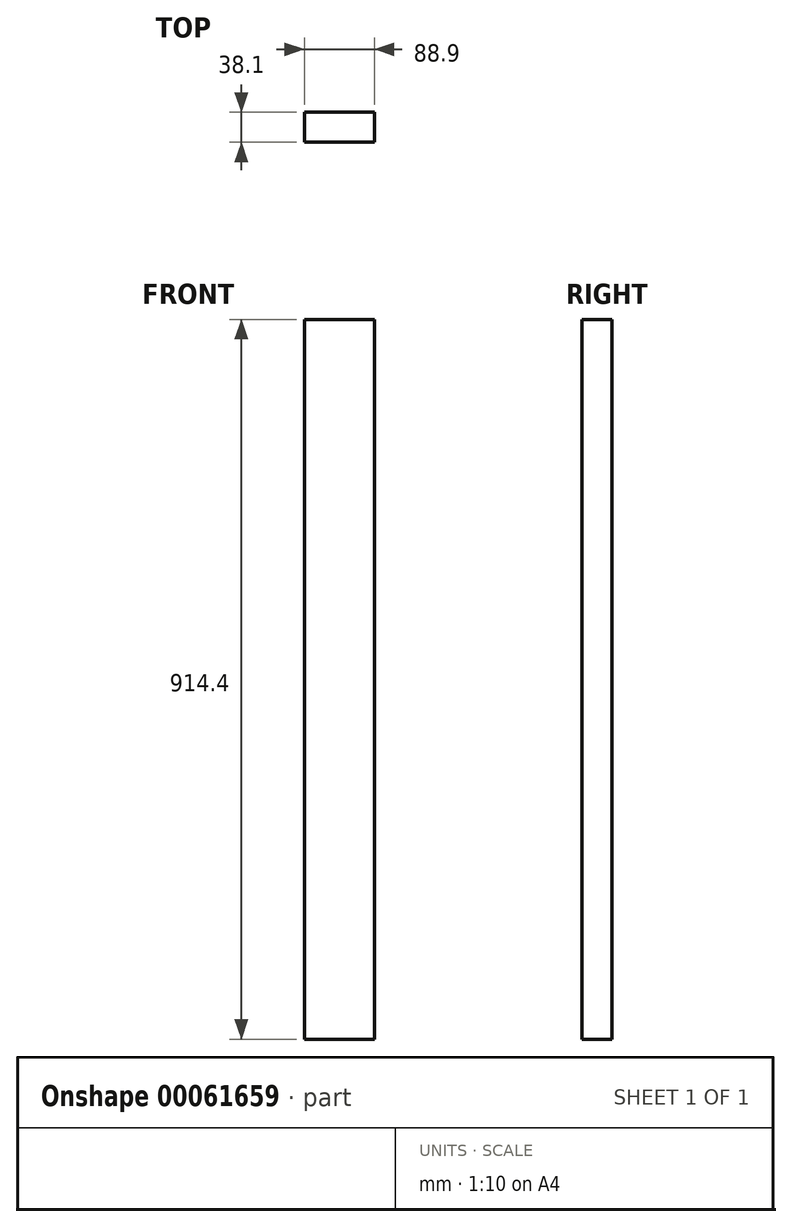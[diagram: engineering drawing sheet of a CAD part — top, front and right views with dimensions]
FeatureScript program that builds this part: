
annotation { "Feature Type Name" : "Feature", "Feature Type Description" : "" }
export const myFeature = defineFeature(function(context is Context, id is Id, definition is map)
    precondition{}
    {
        {
            var Q0;
            Q0=qCreatedBy(makeId("Top.planeOp"),FACE);
            var sketch = newSketch(context, id + "F0", { "sketchPlane" : qUnion([Q0])});
            skLineSegment(sketch, "E0.bottom", {"start": v(0, 0) * mm, "end": v(88.9, 0) * mm});
            skLineSegment(sketch, "E0.top", {"start": v(0, 38.1) * mm, "end": v(88.9, 38.1) * mm});
            skLineSegment(sketch, "E0.left", {"start": v(0, 0) * mm, "end": v(0, 38.1) * mm});
            skLineSegment(sketch, "E0.right", {"start": v(88.9, 0) * mm, "end": v(88.9, 38.1) * mm});
            skSolve(sketch);
        }
        {
            var Q0;
            Q0 = qSketchRegion(id + "F0", true);
            extrude(context, id + "F1", {"entities" : qUnion([Q0]), "depth" : 914.4 * mm});
        }
    });
